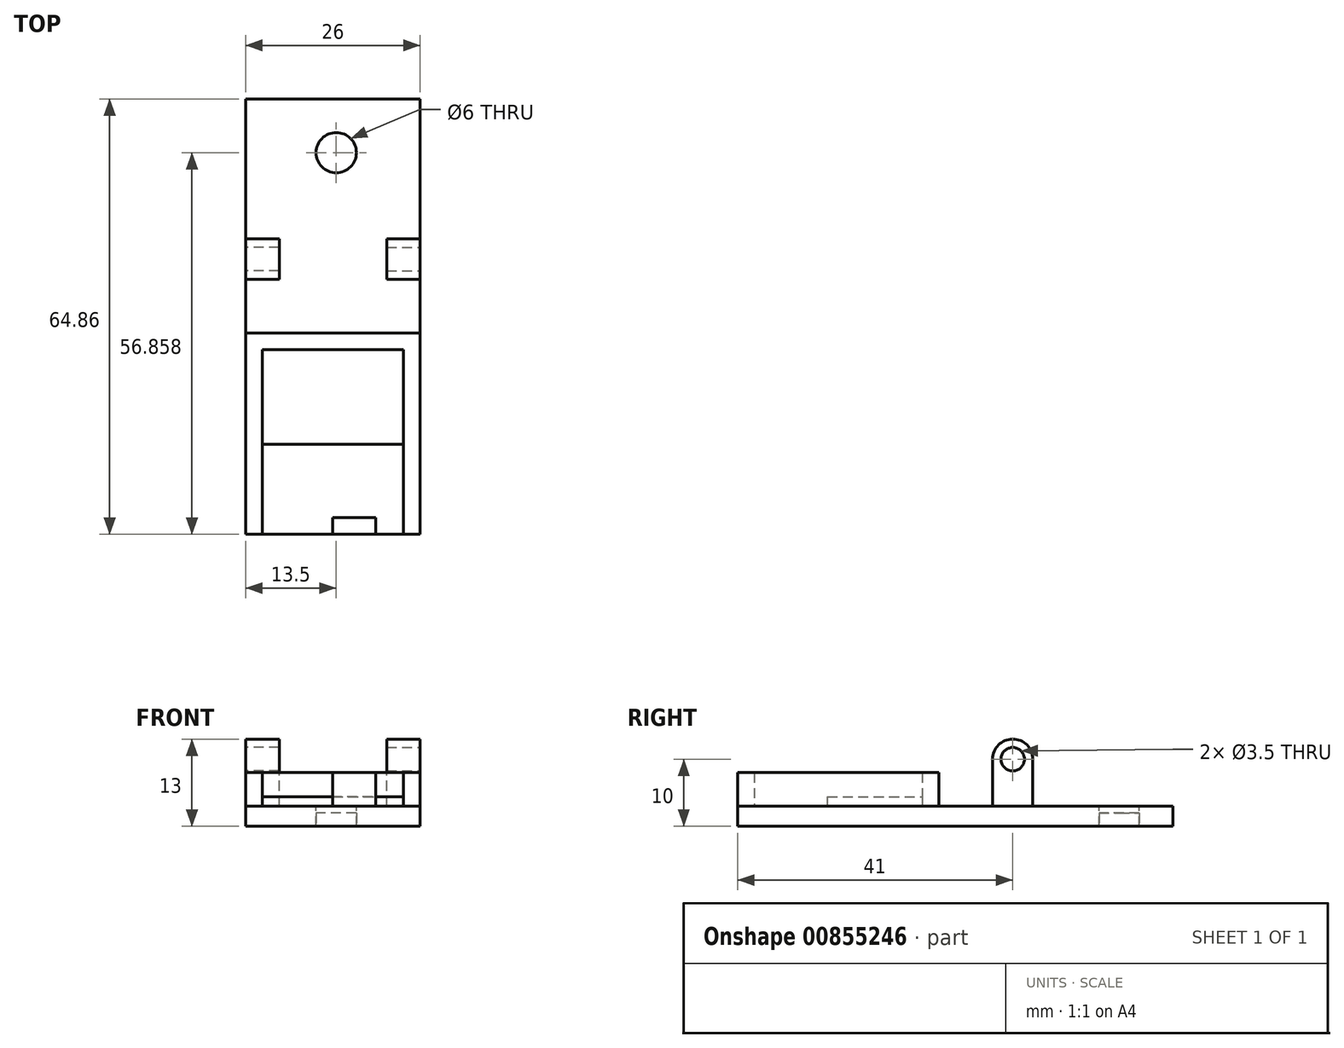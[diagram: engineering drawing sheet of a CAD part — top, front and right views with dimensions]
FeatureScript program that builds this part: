
annotation { "Feature Type Name" : "Feature", "Feature Type Description" : "" }
export const myFeature = defineFeature(function(context is Context, id is Id, definition is map)
    precondition{}
    {
        {
            var Q0;
            Q0=qCreatedBy(makeId("Top.planeOp"),FACE);
            var sketch = newSketch(context, id + "F0", { "sketchPlane" : qUnion([Q0])});
            skLineSegment(sketch, "E0.bottom", {"start": v(0, 0) * mm, "end": v(-21, 0) * mm});
            skLineSegment(sketch, "E0.top", {"start": v(0, 25) * mm, "end": v(-21, 25) * mm});
            skLineSegment(sketch, "E0.left", {"start": v(0, 0) * mm, "end": v(0, 25) * mm});
            skLineSegment(sketch, "E0.right", {"start": v(-21, 0) * mm, "end": v(-21, 25) * mm});
            skLineSegment(sketch, "E1.0", {"start": v(2.5, 27.5) * mm, "end": v(-23.5, 27.5) * mm});
            skLineSegment(sketch, "E1.1", {"start": v(2.5, -2.5) * mm, "end": v(2.5, 27.5) * mm});
            skLineSegment(sketch, "E1.2", {"start": v(2.5, -2.5) * mm, "end": v(-23.5, -2.5) * mm});
            skLineSegment(sketch, "E1.3", {"start": v(-23.5, -2.5) * mm, "end": v(-23.5, 27.5) * mm});
            skLineSegment(sketch, "E2.bottom", {"start": v(-21, 0) * mm, "end": v(-15.95, 0) * mm});
            skLineSegment(sketch, "E2.top", {"start": v(-21, -2.5) * mm, "end": v(-15.95, -2.5) * mm});
            skLineSegment(sketch, "E2.left", {"start": v(-21, 0) * mm, "end": v(-21, -2.5) * mm});
            skLineSegment(sketch, "E2.right", {"start": v(-15.95, 0) * mm, "end": v(-15.95, -2.5) * mm});
            skLineSegment(sketch, "E3.bottom", {"start": v(-4.14, 0) * mm, "end": v(0, 0) * mm});
            skLineSegment(sketch, "E3.top", {"start": v(-4.14, -2.5) * mm, "end": v(0, -2.5) * mm});
            skLineSegment(sketch, "E3.left", {"start": v(-4.14, 0) * mm, "end": v(-4.14, -2.5) * mm});
            skLineSegment(sketch, "E3.right", {"start": v(0, 0) * mm, "end": v(0, -2.5) * mm});
            skLineSegment(sketch, "E4.bottom", {"start": v(-21, 25) * mm, "end": v(0, 25) * mm});
            skLineSegment(sketch, "E4.top", {"start": v(-21, 10.89) * mm, "end": v(0, 10.89) * mm});
            skLineSegment(sketch, "E4.left", {"start": v(-21, 25) * mm, "end": v(-21, 10.89) * mm});
            skLineSegment(sketch, "E4.right", {"start": v(0, 25) * mm, "end": v(0, 10.89) * mm});
            skLineSegment(sketch, "E5.bottom", {"start": v(-10.54, 0) * mm, "end": v(-4.14, 0) * mm});
            skLineSegment(sketch, "E5.top", {"start": v(-10.54, -2.5) * mm, "end": v(-4.14, -2.5) * mm});
            skLineSegment(sketch, "E5.left", {"start": v(-10.54, 0) * mm, "end": v(-10.54, -2.5) * mm});
            skLineSegment(sketch, "E6.bottom", {"start": v(-23.5, 27.5) * mm, "end": v(2.5, 27.5) * mm});
            skLineSegment(sketch, "E6.top", {"start": v(-23.5, 62.36) * mm, "end": v(2.5, 62.36) * mm});
            skLineSegment(sketch, "E6.left", {"start": v(-23.5, 27.5) * mm, "end": v(-23.5, 62.36) * mm});
            skLineSegment(sketch, "E6.right", {"start": v(2.5, 27.5) * mm, "end": v(2.5, 62.36) * mm});
            skCircle(sketch, "E7", {"center": v(-10, 54.36) * mm, "radius": 3 * mm});
            skSolve(sketch);
        }
        {
            var Q0;
            {var subQ0=makeQuery(id+"F0.imprint","IMPRINT",EDGE,{"derivedFrom":sQuery(id+"F0.wireOp",EDGE,"E1.0")});var subQ1=sQuery(id+"F0.wireOp",EDGE,"E2.left");var subQ5=sQuery(id+"F0.wireOp",EDGE,"E2.right");var subQ10=makeQuery(id+"F0.imprint","IMPRINT",EDGE,{"derivedFrom":subQ1});var subQ11=makeQuery(id+"F0.imprint","IMPRINT",EDGE,{"derivedFrom":subQ5});var subQ17=sQuery(id+"F0.wireOp",EDGE,"E0.top");var subQ27=sQuery(id+"F0.wireOp",EDGE,"E3.left");var subQ30=makeQuery(id+"F0.imprint","IMPRINT",EDGE,{"derivedFrom":subQ27});Q0=qUnion([makeQuery(id+"F0.imprint","IMPRINT",FACE,{"disambiguationData":[TD([[subQ30,-1.0]])]}),makeQuery(id+"F0.imprint","IMPRINT",FACE,{"disambiguationData":[TD([[subQ30,1.0]])]}),makeQuery(id+"F0.imprint","IMPRINT",FACE,{"disambiguationData":[TD([[subQ11,1.0]])]}),makeQuery(id+"F0.imprint","IMPRINT",FACE,{"disambiguationData":[TD([[makeQuery(id+"F0.imprint","IMPRINT",EDGE,{"derivedFrom":subQ17}),-1.0]])]}),makeQuery(id+"F0.imprint","IMPRINT",FACE,{"disambiguationData":[TD([[subQ10,1.0]])]}),makeQuery(id+"F0.imprint","IMPRINT",FACE,{"disambiguationData":[TD([[subQ0,-1.0]])]})]);}
            var Q1;
            {var subQ0=sQuery(id+"F0.wireOp",EDGE,"E0.top");Q1=makeQuery(id+"F0.imprint","IMPRINT",FACE,{"disambiguationData":[TD([[makeQuery(id+"F0.imprint","IMPRINT",EDGE,{"derivedFrom":subQ0}),1.0]])]});}
            var Q2;
            {var subQ8=sQuery(id+"F0.wireOp",EDGE,"E4.top");Q2=makeQuery(id+"F0.imprint","IMPRINT",FACE,{"disambiguationData":[TD([[makeQuery(id+"F0.imprint","IMPRINT",EDGE,{"derivedFrom":subQ8}),-1.0]])]});}
            extrude(context, id + "F1", {"entities" : qUnion([Q0, Q1, Q2]), "oppositeDirection" : true, "depth" : 3 * mm, "offsetDistance" : 25 * mm});
        }
        {
            var Q0;
            {var subQ8=sQuery(id+"F0.wireOp",EDGE,"E0.top");Q0=makeQuery(id+"F0.imprint","IMPRINT",FACE,{"disambiguationData":[TD([[makeQuery(id+"F0.imprint","IMPRINT",EDGE,{"derivedFrom":subQ8}),-1.0]])]});}
            var Q1;
            {var subQ0=sQuery(id+"F0.wireOp",EDGE,"E3.left");Q1=makeQuery(id+"F0.imprint","IMPRINT",FACE,{"disambiguationData":[TD([[makeQuery(id+"F0.imprint","IMPRINT",EDGE,{"derivedFrom":subQ0}),-1.0]])]});}
            extrude(context, id + "F2", {"entities" : qUnion([Q0, Q1]), "depth" : 5 * mm, "offsetDistance" : 25 * mm});
        }
        {
            var Q0;
            {var subQ0=sQuery(id+"F0.wireOp",EDGE,"E0.top");Q0=makeQuery(id+"F0.imprint","IMPRINT",FACE,{"disambiguationData":[TD([[makeQuery(id+"F0.imprint","IMPRINT",EDGE,{"derivedFrom":subQ0}),1.0]])]});}
            extrude(context, id + "F3", {"entities" : qUnion([Q0]), "depth" : 1.4 * mm, "offsetDistance" : 25 * mm});
        }
        {
            var Q0;
            Q0=makeQuery(id+"F1.opExtrude","SWEPT_FACE",FACE,{"disambiguationData":[OSD([sQuery(id+"F0.wireOp",EDGE,"E1.1"),sQuery(id+"F0.wireOp",EDGE,"E6.right")])]});
            var sketch = newSketch(context, id + "F4", { "sketchPlane" : qUnion([Q0])});
            skLineSegment(sketch, "E8.bottom", {"start": v(35.5, 0) * mm, "end": v(41.5, 0) * mm});
            skLineSegment(sketch, "E8.top", {"start": v(35.5, 7) * mm, "end": v(41.5, 7) * mm});
            skLineSegment(sketch, "E8.left", {"start": v(35.5, 0) * mm, "end": v(35.5, 7) * mm});
            skLineSegment(sketch, "E8.right", {"start": v(41.5, 0) * mm, "end": v(41.5, 7) * mm});
            skArc(sketch, "E9", {"start": v(41.5, 7) * mm, "mid": v(38.5, 10) * mm, "end": v(35.5, 7) * mm});
            skCircle(sketch, "E10", {"center": v(38.5, 7) * mm, "radius": 1.75 * mm});
            skSolve(sketch);
        }
        {
            var Q0;
            {var subQ0=sQuery(id+"F4.wireOp",EDGE,"E9");Q0=makeQuery(id+"F4.imprint","IMPRINT",FACE,{"disambiguationData":[TD([[makeQuery(id+"F4.imprint","IMPRINT",EDGE,{"derivedFrom":subQ0}),1.0]])]});}
            var Q1;
            Q1=makeQuery(id+"F4.imprint","IMPRINT",FACE,{"disambiguationData":[TD([[makeQuery(id+"F4.imprint","IMPRINT",EDGE,{"derivedFrom":sQuery(id+"F4.wireOp",EDGE,"E8.bottom")}),1.0]])]});
            extrude(context, id + "F5", {"entities" : qUnion([Q0, Q1]), "oppositeDirection" : true, "depth" : 5 * mm, "offsetDistance" : 25 * mm});
        }
        {
            var Q0;
            Q0=makeQuery(id+"F1.opExtrude","SWEPT_FACE",FACE,{"disambiguationData":[OSD([sQuery(id+"F0.wireOp",EDGE,"E1.3"),sQuery(id+"F0.wireOp",EDGE,"E6.left")])]});
            var sketch = newSketch(context, id + "F6", { "sketchPlane" : qUnion([Q0])});
            skLineSegment(sketch, "E11.bottom", {"start": v(-41.5, 0) * mm, "end": v(-35.5, 0) * mm});
            skLineSegment(sketch, "E11.top", {"start": v(-41.5, 7) * mm, "end": v(-35.5, 7) * mm});
            skLineSegment(sketch, "E11.left", {"start": v(-41.5, 0) * mm, "end": v(-41.5, 7) * mm});
            skLineSegment(sketch, "E11.right", {"start": v(-35.5, 0) * mm, "end": v(-35.5, 7) * mm});
            skArc(sketch, "E12", {"start": v(-35.5, 7) * mm, "mid": v(-38.5, 10) * mm, "end": v(-41.5, 7) * mm});
            skCircle(sketch, "E13", {"center": v(-38.5, 7) * mm, "radius": 1.75 * mm});
            skSolve(sketch);
        }
        {
            var Q0;
            Q0=qSketchRegion(id+"F6",true);
            extrude(context, id + "F7", {"entities" : qUnion([Q0]), "operationType" : NewBodyOperationType.ADD, "oppositeDirection" : true, "depth" : 5 * mm, "offsetDistance" : 25 * mm});
        }
        {
            var Q0;
            Q0=makeQuery(id+"F1.opExtrude","CAP_FACE",FACE,{"disambiguationData":[OSD([sQuery(id+"F0.wireOp",EDGE,"E1.1"),sQuery(id+"F0.wireOp",EDGE,"E1.2"),sQuery(id+"F0.wireOp",EDGE,"E1.3"),sQuery(id+"F0.wireOp",EDGE,"E6.top"),sQuery(id+"F0.wireOp",EDGE,"E6.left"),sQuery(id+"F0.wireOp",EDGE,"E6.right"),sQuery(id+"F0.wireOp",EDGE,"E7")])],"isStart":false});
            var sketch = newSketch(context, id + "F8", { "sketchPlane" : qUnion([Q0])});
            skCircle(sketch, "E14", {"center": v(-10, -54.36) * mm, "radius": 3 * mm});
            skSolve(sketch);
        }
        {
            var Q0;
            Q0=qSketchRegion(id+"F8",true);
            extrude(context, id + "F9", {"entities" : qUnion([Q0]), "oppositeDirection" : true, "depth" : 2 * mm, "offsetDistance" : 25 * mm});
        }
    });
